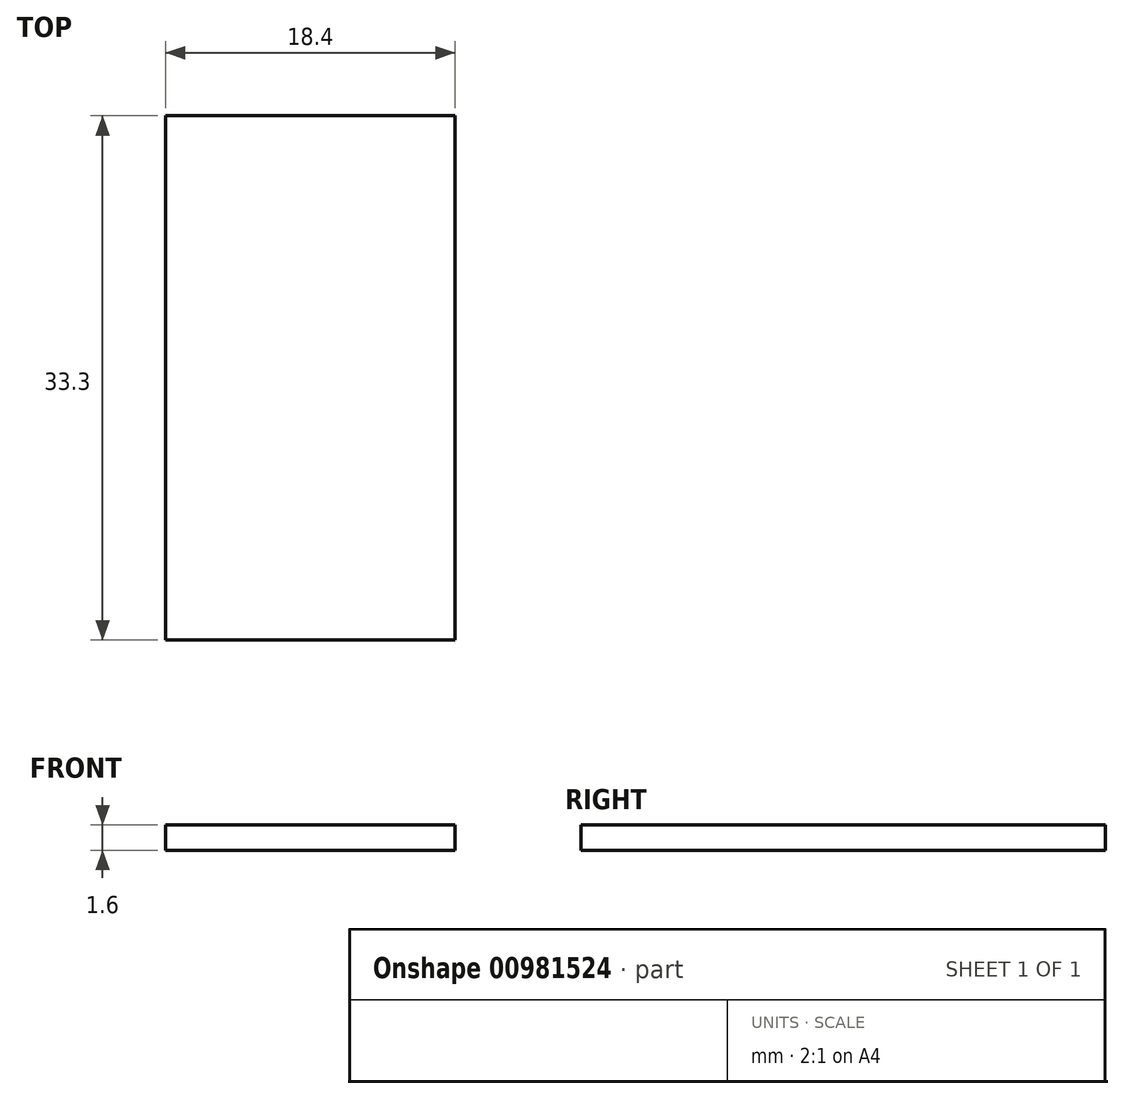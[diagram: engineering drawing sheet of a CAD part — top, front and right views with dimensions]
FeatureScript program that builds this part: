
annotation { "Feature Type Name" : "Feature", "Feature Type Description" : "" }
export const myFeature = defineFeature(function(context is Context, id is Id, definition is map)
    precondition{}
    {
        {
            var Q0;
            Q0=qCreatedBy(makeId("Top.planeOp"),FACE);
            var sketch = newSketch(context, id + "F0", { "sketchPlane" : qUnion([Q0])});
            skLineSegment(sketch, "E0.bottom", {"start": v(-9.2, 16.65) * mm, "end": v(9.2, 16.65) * mm});
            skLineSegment(sketch, "E0.top", {"start": v(-9.2, -16.65) * mm, "end": v(9.2, -16.65) * mm});
            skLineSegment(sketch, "E0.left", {"start": v(-9.2, 16.65) * mm, "end": v(-9.2, -16.65) * mm});
            skLineSegment(sketch, "E0.right", {"start": v(9.2, 16.65) * mm, "end": v(9.2, -16.65) * mm});
            skPoint(sketch, "E0.middle", {"position": v(0, 0) * mm});
            skSolve(sketch);
        }
        {
            var Q0;
            Q0=makeQuery(id+"F0.imprint","IMPRINT",FACE,{"disambiguationData":[TD([[makeQuery(id+"F0.imprint","IMPRINT",EDGE,{"derivedFrom":sQuery(id+"F0.wireOp",EDGE,"E0.bottom")}),-1.0]])]});
            extrude(context, id + "F1", {"entities" : qUnion([Q0]), "depth" : 1.6 * mm, "offsetDistance" : 25 * mm});
        }
    });
